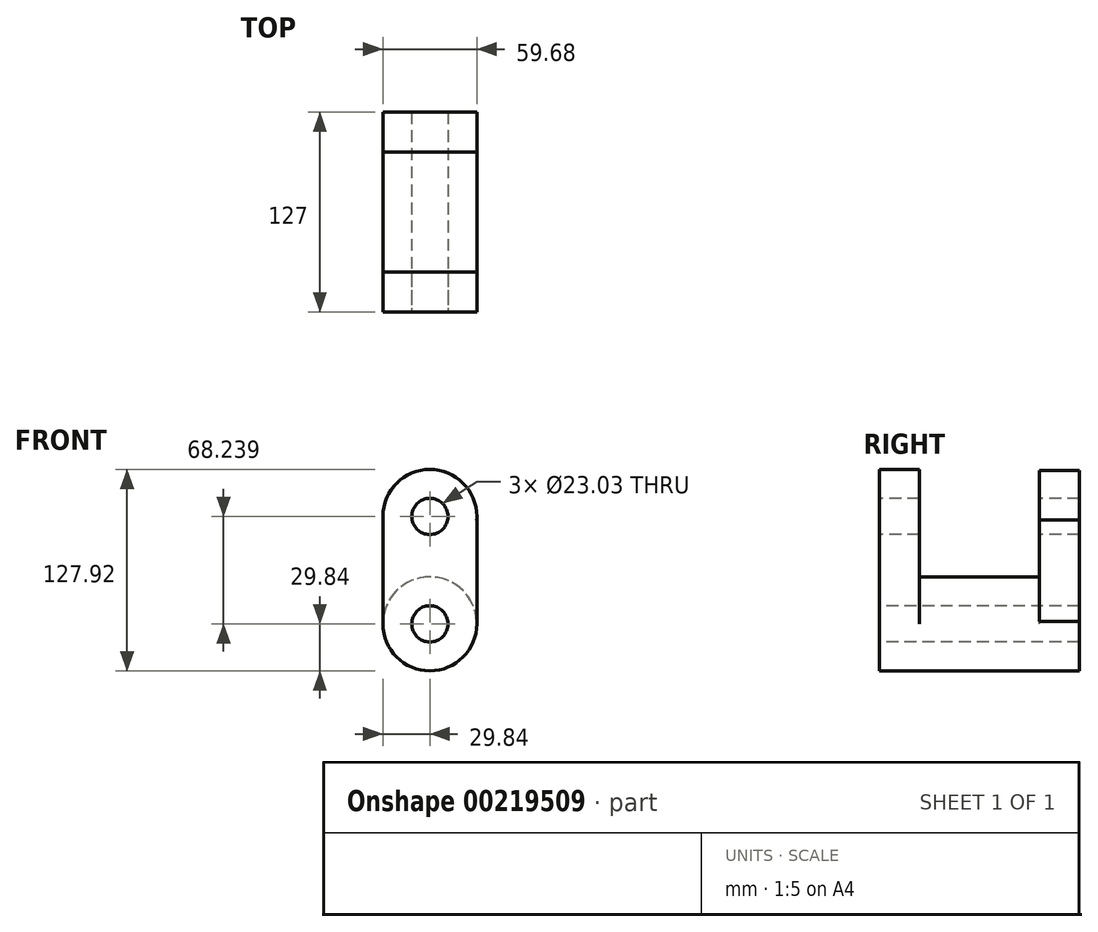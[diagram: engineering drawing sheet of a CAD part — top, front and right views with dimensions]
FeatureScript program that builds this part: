
annotation { "Feature Type Name" : "Feature", "Feature Type Description" : "" }
export const myFeature = defineFeature(function(context is Context, id is Id, definition is map)
    precondition{}
    {
        {
            var Q0;
            Q0=qCreatedBy(makeId("Front.planeOp"),FACE);
            var sketch = newSketch(context, id + "F0", { "sketchPlane" : qUnion([Q0])});
            skCircle(sketch, "E0", {"center": v(0, -34.12) * mm, "radius": 29.84 * mm});
            skSolve(sketch);
        }
        {
            var Q0;
            Q0 = qSketchRegion(id + "F0", true);
            extrude(context, id + "F1", {"entities" : qUnion([Q0]), "depth" : 127 * mm});
        }
        {
            var Q0;
            Q0=makeQuery(id+"F1.opExtrude","CAP_FACE",FACE,{"disambiguationData":[OSD([sQuery(id+"F0.wireOp",EDGE,"E0")])],"isStart":false});
            var sketch = newSketch(context, id + "F2", { "sketchPlane" : qUnion([Q0])});
            skLineSegment(sketch, "E1", {"start": v(0, -34.12) * mm, "end": v(-29.84, -34.12) * mm});
            skLineSegment(sketch, "E2", {"start": v(0, -34.12) * mm, "end": v(29.84, -34.12) * mm});
            skArc(sketch, "E3", {"start": v(11.51, -34.12) * mm, "mid": v(0, -22.6) * mm, "end": v(-11.51, -34.12) * mm});
            skArc(sketch, "E4", {"start": v(29.84, -34.12) * mm, "mid": v(0, -4.28) * mm, "end": v(-29.84, -34.12) * mm});
            skArc(sketch, "E5.MirrorC", {"start": v(-29.84, 34.12) * mm, "mid": v(0, 63.96) * mm, "end": v(29.84, 34.12) * mm});
            skArc(sketch, "E6.MirrorC", {"start": v(-11.51, 34.12) * mm, "mid": v(0, 45.63) * mm, "end": v(11.51, 34.12) * mm});
            skLineSegment(sketch, "E7.top", {"start": v(29.84, -34.12) * mm, "end": v(-29.84, -34.12) * mm});
            skLineSegment(sketch, "E7.left", {"start": v(29.84, 34.12) * mm, "end": v(29.84, -34.12) * mm});
            skLineSegment(sketch, "E7.right", {"start": v(-29.84, 34.12) * mm, "end": v(-29.84, -34.12) * mm});
            skArc(sketch, "E8.MirrorCS", {"start": v(-11.51, 34.12) * mm, "mid": v(0, 22.6) * mm, "end": v(11.51, 34.12) * mm});
            skSolve(sketch);
        }
        {
            var Q0;
            Q0 = qSketchRegion(id + "F2", true);
            extrude(context, id + "F3", {"entities" : qUnion([Q0]), "operationType" : NewBodyOperationType.ADD, "oppositeDirection" : true, "depth" : 25.4 * mm});
        }
        {
            var Q0;
            Q0=makeQuery(id+"F1.opExtrude","CAP_FACE",FACE,{"disambiguationData":[OSD([sQuery(id+"F0.wireOp",EDGE,"E0")])],"isStart":true});
            var sketch = newSketch(context, id + "F4", { "sketchPlane" : qUnion([Q0])});
            skLineSegment(sketch, "E9", {"start": v(0, -34.12) * mm, "end": v(29.84, -34.12) * mm});
            skLineSegment(sketch, "E10", {"start": v(29.84, -34.12) * mm, "end": v(-29.84, -34.12) * mm});
            skPoint(sketch, "E10.endSnap0", {"position": v(14.92, -34.12) * mm});
            skLineSegment(sketch, "E11.bottom", {"start": v(29.84, -34.12) * mm, "end": v(29.42, -34.12) * mm});
            skLineSegment(sketch, "E11.top", {"start": v(29.84, -29.13) * mm, "end": v(29.42, -29.13) * mm});
            skLineSegment(sketch, "E12.bottom", {"start": v(29.84, -34.12) * mm, "end": v(-29.8, -34.12) * mm});
            skLineSegment(sketch, "E12.left", {"start": v(29.84, -34.12) * mm, "end": v(29.84, 33.52) * mm});
            skLineSegment(sketch, "E12.right", {"start": v(-29.8, -34.12) * mm, "end": v(-29.8, 33.52) * mm});
            skArc(sketch, "E13", {"start": v(29.84, 33.52) * mm, "mid": v(-0.76, 63.35) * mm, "end": v(-29.8, 32) * mm});
            skSolve(sketch);
        }
        {
            var Q0;
            Q0 = qSketchRegion(id + "F4", true);
            extrude(context, id + "F5", {"entities" : qUnion([Q0]), "operationType" : NewBodyOperationType.ADD, "oppositeDirection" : true, "depth" : 25.4 * mm});
        }
        {
            var Q0;
            Q0=makeQuery(id+"F3.boolean.opBoolean","MERGE",FACE,{"derivedFrom":[makeQuery(id+"F1.opExtrude","CAP_FACE",FACE,{"disambiguationData":[OSD([sQuery(id+"F0.wireOp",EDGE,"E0")])],"isStart":false}),makeQuery(id+"F3.opExtrude","CAP_FACE",FACE,{"disambiguationData":[OSD([sQuery(id+"F2.wireOp",EDGE,"E5.MirrorC"),sQuery(id+"F2.wireOp",EDGE,"E6.MirrorC"),sQuery(id+"F2.wireOp",EDGE,"E7.top"),sQuery(id+"F2.wireOp",EDGE,"E7.left"),sQuery(id+"F2.wireOp",EDGE,"E7.right"),sQuery(id+"F2.wireOp",EDGE,"E8.MirrorCS")])],"isStart":true})]});
            var sketch = newSketch(context, id + "F6", { "sketchPlane" : qUnion([Q0])});
            skCircle(sketch, "E14", {"center": v(0, 34.12) * mm, "radius": 11.51 * mm});
            skCircle(sketch, "E15.MirrorC", {"center": v(0, -34.12) * mm, "radius": 11.51 * mm});
            skSolve(sketch);
        }
        {
            var Q0;
            Q0 = qSketchRegion(id + "F6", true);
            extrude(context, id + "F7", {"entities" : qUnion([Q0]), "operationType" : NewBodyOperationType.REMOVE, "oppositeDirection" : true, "depth" : 249.17 * mm});
        }
    });
